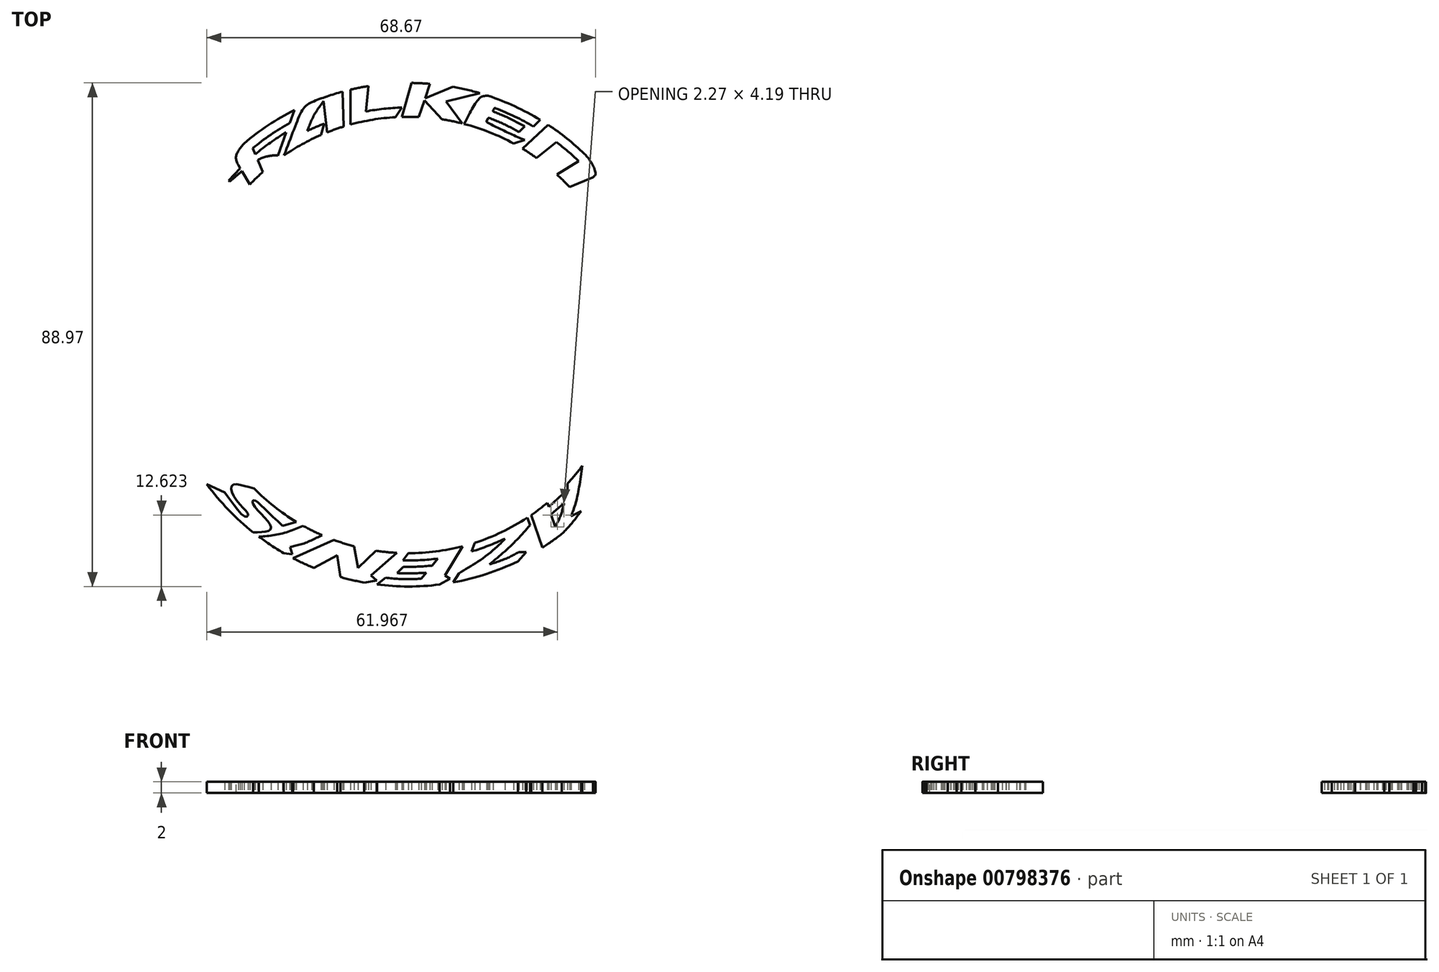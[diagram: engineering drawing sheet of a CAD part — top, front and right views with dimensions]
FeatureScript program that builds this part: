
annotation { "Feature Type Name" : "Feature", "Feature Type Description" : "" }
export const myFeature = defineFeature(function(context is Context, id is Id, definition is map)
    precondition{}
    {
        {
            var Q0;
            Q0=qCreatedBy(makeId("Top.planeOp"),FACE);
            var sketch = newSketch(context, id + "F0", { "sketchPlane" : qUnion([Q0])});
            skArc(sketch, "E0", {"start": v(28.48, 26.41) * mm, "mid": v(27.4, 27.54) * mm, "end": v(26.26, 28.63) * mm});
            skArc(sketch, "E1", {"start": v(31.1, 32.28) * mm, "mid": v(28, 35) * mm, "end": v(24.68, 37.42) * mm});
            skArc(sketch, "E2.trimOffspring", {"start": v(-25.73, 29.1) * mm, "mid": v(-26.9, 28.02) * mm, "end": v(-28.03, 26.89) * mm});
            skArc(sketch, "E3.trimOffspring", {"start": v(-15.48, 35.63) * mm, "mid": v(-18.81, 33.99) * mm, "end": v(-21.98, 32.03) * mm});
            skArc(sketch, "E4.trimOffspring", {"start": v(-11.44, 37.12) * mm, "mid": v(-12.93, 36.63) * mm, "end": v(-14.4, 36.08) * mm});
            skArc(sketch, "E5.trimOffspring", {"start": v(-2.33, 38.78) * mm, "mid": v(-6.34, 38.32) * mm, "end": v(-10.28, 37.46) * mm});
            skArc(sketch, "E6.trimOffspring", {"start": v(1.84, 38.8) * mm, "mid": v(0.34, 38.84) * mm, "end": v(-1.15, 38.83) * mm});
            skArc(sketch, "E7.trimOffspring", {"start": v(18.59, 34.1) * mm, "mid": v(14.32, 36.1) * mm, "end": v(9.84, 37.58) * mm});
            skArc(sketch, "E8.trimOffspring", {"start": v(22.65, 31.56) * mm, "mid": v(21.41, 32.41) * mm, "end": v(20.14, 33.22) * mm});
            skArc(sketch, "E9.trimOffspring", {"start": v(9.5, 37.67) * mm, "mid": v(7.73, 38.07) * mm, "end": v(5.94, 38.39) * mm});
            skLineSegment(sketch, "E10", {"start": v(-28.03, 26.89) * mm, "end": v(-29.44, 29.23) * mm});
            skLineSegment(sketch, "E11", {"start": v(28.48, 26.41) * mm, "end": v(32.6, 28.18) * mm});
            skLineSegment(sketch, "E12", {"start": v(-25.73, 29.1) * mm, "end": v(-26.64, 31.2) * mm});
            skLineSegment(sketch, "E13", {"start": v(-20.18, 40.03) * mm, "end": v(-21, 37.74) * mm});
            skLineSegment(sketch, "E14", {"start": v(-11.44, 37.12) * mm, "end": v(-11.67, 43.28) * mm});
            skLineSegment(sketch, "E15", {"start": v(-10.28, 37.46) * mm, "end": v(-10.28, 43.63) * mm});
            skLineSegment(sketch, "E16", {"start": v(-7.06, 44.26) * mm, "end": v(-7.53, 39.79) * mm});
            skLineSegment(sketch, "E17", {"start": v(-14.4, 36.08) * mm, "end": v(-15.02, 41.58) * mm});
            skFitSpline(sketch, "E18", {"points": [v(-15.02, 41.58) * mm, v(-16.7, 39.13) * mm, v(-17.9, 36.32) * mm], "startDerivative": vector(-3.62, -4.78) * mm, "endDerivative": vector(-2.11, -5.78) * mm});
            skLineSegment(sketch, "E19", {"start": v(-15.48, 35.63) * mm, "end": v(-14.92, 37.65) * mm});
            skFitSpline(sketch, "E20", {"points": [v(-23.09, 31.99) * mm, v(-24.2, 31.99) * mm, v(-26.64, 31.2) * mm, v(-31.6, 27.4) * mm], "startDerivative": vector(-4.99, 0.31) * mm, "endDerivative": vector(-10.73, -9.3) * mm});
            skLineSegment(sketch, "E21", {"start": v(-31.6, 27.4) * mm, "end": v(-31.76, 27.6) * mm});
            skFitSpline(sketch, "E22", {"points": [v(-21.98, 32.03) * mm, v(-19.79, 37.78) * mm, v(-18.44, 40.45) * mm, v(-17.08, 41.44) * mm], "startDerivative": vector(5.17, 13.69) * mm, "endDerivative": vector(6.22, 3.24) * mm});
            skArc(sketch, "E23.trimOffspring", {"start": v(-20.18, 40.03) * mm, "mid": v(-24.8, 37.34) * mm, "end": v(-29.05, 34.13) * mm});
            skArc(sketch, "E24.trimOffspring", {"start": v(-21, 37.74) * mm, "mid": v(-24.38, 35.65) * mm, "end": v(-27.54, 33.27) * mm});
            skArc(sketch, "E25.trimOffspring", {"start": v(-21.6, 36.11) * mm, "mid": v(-24.41, 34.27) * mm, "end": v(-27.08, 32.2) * mm});
            skLineSegment(sketch, "E26.trimOffspring", {"start": v(-21.6, 36.11) * mm, "end": v(-23.09, 31.99) * mm});
            skLineSegment(sketch, "E27.trimOffspring", {"start": v(-27.08, 32.2) * mm, "end": v(-27.54, 33.27) * mm});
            skLineSegment(sketch, "E28.trimOffspring", {"start": v(-29.75, 29.75) * mm, "end": v(-30.07, 30.28) * mm});
            skArc(sketch, "E29.trimOffspring", {"start": v(-11.67, 43.28) * mm, "mid": v(-14.4, 42.45) * mm, "end": v(-17.08, 41.44) * mm});
            skArc(sketch, "E30.trimOffspring", {"start": v(-14.92, 37.65) * mm, "mid": v(-16.42, 37.01) * mm, "end": v(-17.9, 36.32) * mm});
            skLineSegment(sketch, "E31", {"start": v(-1.15, 38.83) * mm, "end": v(0.57, 44.82) * mm});
            skLineSegment(sketch, "E32", {"start": v(1.84, 38.8) * mm, "end": v(2.8, 41.73) * mm});
            skLineSegment(sketch, "E33", {"start": v(-1.15, 40.48) * mm, "end": v(-2.33, 38.78) * mm});
            skArc(sketch, "E34.trimOffspring", {"start": v(-1.15, 40.48) * mm, "mid": v(-4.36, 40.26) * mm, "end": v(-7.53, 39.79) * mm});
            skArc(sketch, "E35.trimOffspring", {"start": v(-7.06, 44.26) * mm, "mid": v(-8.68, 43.98) * mm, "end": v(-10.28, 43.63) * mm});
            skLineSegment(sketch, "E36", {"start": v(5.94, 38.39) * mm, "end": v(2.8, 41.73) * mm});
            skLineSegment(sketch, "E37", {"start": v(7.84, 44.13) * mm, "end": v(2.94, 42.14) * mm});
            skLineSegment(sketch, "E38", {"start": v(9.5, 37.67) * mm, "end": v(6.67, 41.54) * mm});
            skLineSegment(sketch, "E39", {"start": v(12.6, 43.02) * mm, "end": v(6.67, 41.54) * mm});
            skLineSegment(sketch, "E40.trimOffspring", {"start": v(2.94, 42.14) * mm, "end": v(3.77, 44.67) * mm});
            skArc(sketch, "E41.trimOffspring", {"start": v(3.77, 44.67) * mm, "mid": v(2.17, 44.77) * mm, "end": v(0.57, 44.82) * mm});
            skFitSpline(sketch, "E42", {"points": [v(9.84, 37.58) * mm, v(11.6, 40.83) * mm, v(12.75, 42.27) * mm, v(13.52, 42.53) * mm, v(14.09, 42.55) * mm], "startDerivative": vector(4.58, 9) * mm, "endDerivative": vector(3.56, -0.32) * mm});
            skArc(sketch, "E43.trimOffspring", {"start": v(12.6, 43.02) * mm, "mid": v(10.24, 43.64) * mm, "end": v(7.84, 44.13) * mm});
            skLineSegment(sketch, "E44", {"start": v(23.27, 38.3) * mm, "end": v(22.09, 37.11) * mm});
            skLineSegment(sketch, "E45", {"start": v(20.14, 33.22) * mm, "end": v(24.68, 37.42) * mm});
            skArc(sketch, "E46.trimOffspring", {"start": v(23.27, 38.3) * mm, "mid": v(18.8, 40.7) * mm, "end": v(14.09, 42.55) * mm});
            skArc(sketch, "E47.trimOffspring", {"start": v(22.09, 37.11) * mm, "mid": v(18.8, 38.89) * mm, "end": v(15.35, 40.37) * mm});
            skLineSegment(sketch, "E48", {"start": v(18.59, 34.1) * mm, "end": v(20.52, 34.73) * mm});
            skLineSegment(sketch, "E49", {"start": v(19.53, 36.17) * mm, "end": v(20.55, 37.16) * mm});
            skFitSpline(sketch, "E50", {"points": [v(19.53, 36.17) * mm, v(16.83, 37.55) * mm, v(14.11, 38.68) * mm], "startDerivative": vector(-5.35, 2.93) * mm, "endDerivative": vector(-5.48, 2.09) * mm});
            skFitSpline(sketch, "E51", {"points": [v(20.52, 34.73) * mm, v(16.78, 36.42) * mm, v(13.75, 37.95) * mm], "startDerivative": vector(-7.68, 3.21) * mm, "endDerivative": vector(-5.82, 3.23) * mm});
            skFitSpline(sketch, "E52", {"points": [v(20.55, 37.16) * mm, v(17.46, 38.73) * mm, v(14.85, 39.83) * mm], "startDerivative": vector(-5.98, 3.17) * mm, "endDerivative": vector(-5.42, 2.15) * mm});
            skLineSegment(sketch, "E53", {"start": v(13.82, 38.1) * mm, "end": v(14.04, 38.54) * mm});
            skLineSegment(sketch, "E54", {"start": v(14.96, 40.01) * mm, "end": v(15.14, 40.3) * mm});
            skPoint(sketch, "E55.visualSharp", {"position": v(15.22, 40.42) * mm});
            skArc(sketch, "E55.filletArc", {"start": v(15.35, 40.37) * mm, "mid": v(15.23, 40.37) * mm, "end": v(15.14, 40.3) * mm});
            skArc(sketch, "E56.filletArc", {"start": v(14.96, 40.01) * mm, "mid": v(14.94, 39.86) * mm, "end": v(15.05, 39.75) * mm});
            skArc(sketch, "E57.filletArc", {"start": v(14.27, 38.62) * mm, "mid": v(14.14, 38.62) * mm, "end": v(14.04, 38.54) * mm});
            skArc(sketch, "E58.filletArc", {"start": v(13.82, 38.1) * mm, "mid": v(13.81, 37.97) * mm, "end": v(13.9, 37.87) * mm});
            skLineSegment(sketch, "E59", {"start": v(22.65, 31.56) * mm, "end": v(26.15, 34.38) * mm});
            skLineSegment(sketch, "E60", {"start": v(26.26, 28.63) * mm, "end": v(30.1, 30.98) * mm});
            skArc(sketch, "E61.trimOffspring", {"start": v(30.1, 30.98) * mm, "mid": v(28.17, 32.74) * mm, "end": v(26.15, 34.38) * mm});
            skLineSegment(sketch, "E62", {"start": v(-31.76, 27.6) * mm, "end": v(-29.75, 29.75) * mm});
            skPoint(sketch, "E63.1.internal.snap0", {"position": v(-30.48, 30.96) * mm});
            skFitSpline(sketch, "E63", {"points": [v(-30.07, 30.28) * mm, v(-30.48, 31.62) * mm, v(-30.01, 32.89) * mm, v(-29.05, 34.13) * mm], "startDerivative": vector(-1.88, 4.08) * mm, "endDerivative": vector(3.02, 3.4) * mm});
            skPoint(sketch, "E64.orphan", {"position": v(-31.2, 32.18) * mm});
            skFitSpline(sketch, "E65", {"points": [v(31.1, 32.28) * mm, v(32.1, 31.08) * mm, v(32.98, 29.29) * mm, v(32.98, 28.48) * mm, v(32.6, 28.18) * mm], "startDerivative": vector(3.5, -3.6) * mm, "endDerivative": vector(-2.75, -1.47) * mm});
            skSolve(sketch);
        }
        {
            var Q0;
            Q0 = qSketchRegion(id + "F0", true);
            extrude(context, id + "F1", {"entities" : qUnion([Q0]), "depth" : 2 * mm, "offsetDistance" : 25 * mm});
        }
        {
            var Q0;
            Q0=qCreatedBy(makeId("Top.planeOp"),FACE);
            var sketch = newSketch(context, id + "F2", { "sketchPlane" : qUnion([Q0])});
            skArc(sketch, "E66", {"start": v(-27.25, -26.87) * mm, "mid": v(-23.73, -30.03) * mm, "end": v(-19.85, -32.72) * mm});
            skArc(sketch, "E67", {"start": v(-35.62, -26.1) * mm, "mid": v(-31.81, -30.62) * mm, "end": v(-27.43, -34.6) * mm});
            skArc(sketch, "E68", {"start": v(-0.91, -40.67) * mm, "mid": v(1.63, -40.65) * mm, "end": v(4.17, -40.47) * mm});
            skArc(sketch, "E69", {"start": v(-2, -41.79) * mm, "mid": v(0.58, -41.83) * mm, "end": v(3.15, -41.72) * mm});
            skArc(sketch, "E70.trimOffspring", {"start": v(28.13, -25.95) * mm, "mid": v(29.45, -24.44) * mm, "end": v(30.7, -22.86) * mm});
            skArc(sketch, "E71.trimOffspring", {"start": v(21.68, -31.54) * mm, "mid": v(23.15, -30.48) * mm, "end": v(24.56, -29.35) * mm});
            skArc(sketch, "E72.trimOffspring", {"start": v(11.72, -36.44) * mm, "mid": v(16.5, -34.54) * mm, "end": v(20.97, -32.01) * mm});
            skArc(sketch, "E73.trimOffspring", {"start": v(0, -38.27) * mm, "mid": v(4.83, -37.97) * mm, "end": v(9.59, -37.05) * mm});
            skArc(sketch, "E74.trimOffspring", {"start": v(-5.75, -37.84) * mm, "mid": v(-3.9, -38.07) * mm, "end": v(-2.05, -38.22) * mm});
            skArc(sketch, "E75.trimOffspring", {"start": v(-13.16, -35.94) * mm, "mid": v(-11.4, -36.54) * mm, "end": v(-9.6, -37.05) * mm});
            skArc(sketch, "E76.trimOffspring", {"start": v(-18.62, -33.44) * mm, "mid": v(-16.98, -34.3) * mm, "end": v(-15.3, -35.08) * mm});
            skFitSpline(sketch, "E77", {"points": [v(30.7, -22.86) * mm, v(29.74, -28.66) * mm, v(28.73, -31.75) * mm], "startDerivative": vector(-1.46, -10.93) * mm, "endDerivative": vector(-2.51, -6.64) * mm});
            skLineSegment(sketch, "E78", {"start": v(28.73, -31.75) * mm, "end": v(30.5, -30.82) * mm});
            skFitSpline(sketch, "E79", {"points": [v(30.5, -30.82) * mm, v(28.94, -32.88) * mm, v(27.11, -34.85) * mm], "startDerivative": vector(-3, -4.24) * mm, "endDerivative": vector(-3.82, -3.76) * mm});
            skLineSegment(sketch, "E80", {"start": v(21.68, -31.54) * mm, "end": v(23.66, -37.28) * mm});
            skLineSegment(sketch, "E81", {"start": v(24.56, -29.35) * mm, "end": v(24.8, -30.07) * mm});
            skLineSegment(sketch, "E82", {"start": v(25.21, -31.38) * mm, "end": v(27.48, -29.43) * mm});
            skFitSpline(sketch, "E83", {"points": [v(27.48, -29.43) * mm, v(26.94, -31.48) * mm, v(25.93, -33.62) * mm], "startDerivative": vector(-0.9, -4.23) * mm, "endDerivative": vector(-2.18, -4.16) * mm});
            skLineSegment(sketch, "E84", {"start": v(28.13, -25.95) * mm, "end": v(28.13, -27.03) * mm});
            skLineSegment(sketch, "E85", {"start": v(28.13, -27.03) * mm, "end": v(24.8, -30.07) * mm});
            skLineSegment(sketch, "E86.trimOffspring", {"start": v(25.21, -31.38) * mm, "end": v(25.93, -33.62) * mm});
            skLineSegment(sketch, "E87", {"start": v(-35.62, -26.1) * mm, "end": v(-32.46, -27.5) * mm});
            skLineSegment(sketch, "E88", {"start": v(11.72, -36.44) * mm, "end": v(11.13, -37.97) * mm});
            skLineSegment(sketch, "E89", {"start": v(7.91, -43.44) * mm, "end": v(8.9, -41.8) * mm});
            skFitSpline(sketch, "E90", {"points": [v(8.9, -41.8) * mm, v(13.04, -39.23) * mm, v(16.54, -36.3) * mm, v(17.03, -35.71) * mm], "startDerivative": vector(9.56, 5.46) * mm, "endDerivative": vector(1.94, 3.07) * mm});
            skLineSegment(sketch, "E91", {"start": v(9.59, -37.05) * mm, "end": v(6.43, -42.21) * mm});
            skLineSegment(sketch, "E92", {"start": v(6.43, -42.21) * mm, "end": v(7.36, -42.79) * mm});
            skLineSegment(sketch, "E93", {"start": v(7.36, -42.79) * mm, "end": v(5.48, -43.81) * mm});
            skArc(sketch, "E94.trimOffspring", {"start": v(7.91, -43.44) * mm, "mid": v(13.74, -41.96) * mm, "end": v(19.31, -39.7) * mm});
            skArc(sketch, "E95.trimOffspring", {"start": v(11.13, -37.97) * mm, "mid": v(14.13, -36.96) * mm, "end": v(17.03, -35.71) * mm});
            skFitSpline(sketch, "E96", {"points": [v(21.74, -33.06) * mm, v(18.37, -36.68) * mm, v(14.35, -40.24) * mm], "startDerivative": vector(-6.63, -7.5) * mm, "endDerivative": vector(-8.13, -6.86) * mm});
            skFitSpline(sketch, "E97", {"points": [v(14.35, -40.24) * mm, v(17.4, -39.16) * mm, v(19.48, -38.1) * mm], "startDerivative": vector(5.94, 1.92) * mm, "endDerivative": vector(4.27, 2.38) * mm});
            skLineSegment(sketch, "E98", {"start": v(19.48, -38.1) * mm, "end": v(20.77, -38.1) * mm});
            skLineSegment(sketch, "E99", {"start": v(20.77, -38.1) * mm, "end": v(19.31, -39.7) * mm});
            skArc(sketch, "E100.trimOffspring", {"start": v(23.66, -37.28) * mm, "mid": v(25.41, -36.1) * mm, "end": v(27.11, -34.85) * mm});
            skLineSegment(sketch, "E101", {"start": v(5.2, -39.22) * mm, "end": v(4.17, -40.47) * mm});
            skLineSegment(sketch, "E102", {"start": v(-0.91, -40.67) * mm, "end": v(-2, -41.79) * mm});
            skLineSegment(sketch, "E103", {"start": v(0, -38.27) * mm, "end": v(-1, -39.55) * mm});
            skLineSegment(sketch, "E104", {"start": v(-2.05, -38.22) * mm, "end": v(-6.6, -42.2) * mm});
            skLineSegment(sketch, "E105", {"start": v(-6.6, -42.2) * mm, "end": v(-5.65, -43.12) * mm});
            skLineSegment(sketch, "E106", {"start": v(-5.65, -43.12) * mm, "end": v(-7.86, -43.45) * mm});
            skLineSegment(sketch, "E107", {"start": v(-5.55, -43.8) * mm, "end": v(-4.05, -42.62) * mm});
            skFitSpline(sketch, "E108", {"points": [v(-4.05, -42.62) * mm, v(-0.56, -42.86) * mm, v(2.29, -42.77) * mm], "startDerivative": vector(6.81, -0.64) * mm, "endDerivative": vector(5.85, 0.36) * mm});
            skArc(sketch, "E109.trimOffspring", {"start": v(-5.55, -43.8) * mm, "mid": v(-0.04, -44.15) * mm, "end": v(5.48, -43.81) * mm});
            skArc(sketch, "E110.trimOffspring", {"start": v(-1, -39.55) * mm, "mid": v(2.1, -39.51) * mm, "end": v(5.2, -39.22) * mm});
            skLineSegment(sketch, "E111", {"start": v(-13.16, -35.94) * mm, "end": v(-20.43, -39.14) * mm});
            skLineSegment(sketch, "E112", {"start": v(-9.6, -37.05) * mm, "end": v(-8.95, -40.87) * mm});
            skLineSegment(sketch, "E113", {"start": v(-5.75, -37.84) * mm, "end": v(-8.95, -40.87) * mm});
            skLineSegment(sketch, "E114", {"start": v(-12.62, -38.67) * mm, "end": v(-16.72, -40.87) * mm});
            skLineSegment(sketch, "E115", {"start": v(-12.62, -38.67) * mm, "end": v(-12.03, -42.48) * mm});
            skArc(sketch, "E116.trimOffspring", {"start": v(-12.03, -42.48) * mm, "mid": v(-9.95, -43.02) * mm, "end": v(-7.86, -43.45) * mm});
            skFitSpline(sketch, "E117", {"points": [v(-15.3, -35.08) * mm, v(-18.14, -36.41) * mm, v(-20.94, -37.22) * mm], "startDerivative": vector(-5.54, -2.77) * mm, "endDerivative": vector(-5.75, -1.5) * mm});
            skLineSegment(sketch, "E118", {"start": v(-20.94, -37.22) * mm, "end": v(-20.5, -38.45) * mm});
            skLineSegment(sketch, "E119", {"start": v(-20.5, -38.45) * mm, "end": v(-22.07, -38.24) * mm});
            skArc(sketch, "E120.trimOffspring", {"start": v(-20.43, -39.14) * mm, "mid": v(-18.6, -40.05) * mm, "end": v(-16.72, -40.87) * mm});
            skFitSpline(sketch, "E121", {"points": [v(-26.42, -35.38) * mm, v(-22.38, -34.8) * mm, v(-18.62, -33.44) * mm], "startDerivative": vector(8.12, 0.66) * mm, "endDerivative": vector(7.42, 3.16) * mm});
            skLineSegment(sketch, "E122.trimOffspring", {"start": v(3.15, -41.72) * mm, "end": v(2.29, -42.77) * mm});
            skFitSpline(sketch, "E123", {"points": [v(-27.43, -34.6) * mm, v(-25.35, -34.46) * mm, v(-24.43, -34.12) * mm, v(-24.39, -33.4) * mm, v(-25.9, -31.46) * mm, v(-27.47, -29.58) * mm, v(-27.5, -28.97) * mm, v(-27.02, -29) * mm, v(-25.71, -30.16) * mm, v(-22.22, -33.44) * mm], "startDerivative": vector(17.57, 0.48) * mm, "endDerivative": vector(20.31, -18.62) * mm});
            skLineSegment(sketch, "E124", {"start": v(-22.22, -33.44) * mm, "end": v(-19.85, -32.72) * mm});
            skFitSpline(sketch, "E125", {"points": [v(-27.25, -26.87) * mm, v(-29.61, -26.22) * mm, v(-30.87, -26.14) * mm, v(-31.3, -26.56) * mm, v(-31.22, -27.5) * mm, v(-29.92, -29.53) * mm, v(-28.63, -30.94) * mm, v(-28.35, -31.47) * mm, v(-28.43, -31.76) * mm, v(-28.94, -31.78) * mm, v(-30.78, -29.8) * mm, v(-32.46, -27.5) * mm], "startDerivative": vector(-20.2, 6.1) * mm, "endDerivative": vector(-11.92, 16.52) * mm});
            skArc(sketch, "E126.trimOffspring", {"start": v(-26.42, -35.38) * mm, "mid": v(-24.29, -36.87) * mm, "end": v(-22.07, -38.24) * mm});
            skLineSegment(sketch, "E127", {"start": v(20.97, -32.01) * mm, "end": v(21.48, -33.35) * mm});
            skSolve(sketch);
        }
        {
            var Q0;
            Q0 = qSketchRegion(id + "F2", true);
            extrude(context, id + "F3", {"entities" : qUnion([Q0]), "depth" : 2 * mm, "offsetDistance" : 25 * mm});
        }
    });
